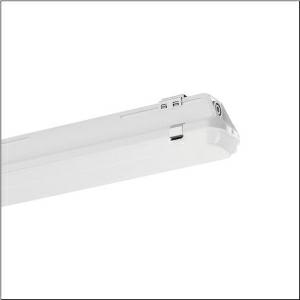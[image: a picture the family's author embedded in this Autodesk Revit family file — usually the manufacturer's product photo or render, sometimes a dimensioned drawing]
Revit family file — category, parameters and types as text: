
# Revit family: monsun_r__11_facade_51ff40mp460h_34d2
name_source: partatom
category: Lighting Fixtures
units: mm (PartAtom-declared; Revit-internal decimal feet)

## family parameters
Cut with Voids When Loaded = No
Host = Face
Light Source = No
Part Type = Normal
Room Calculation Point = No
Round Connector Dimension = Use Diameter
Shared = No

## types (1)
- --- (1 x LED, 6110 lm, 33.5 W, 4000K)
    Apparent Load = 34 VA
    CIE Flux Codes = 47 77 93 95 100
    Color Rendering = 80
    Color Temperature = 4000K
    Default Elevation = 1800 mm
    Description = Monsun® 11 facade, damp-proof luminaire, chain hanger, primary optical cover: enclosure, of PMMA, light emission: direct distribution, primary light characteristic: symmetric, installation type: surface-mounted, horizontal mounting, vertical mounting, LED, rated luminous flux: 6.110lm, luminous efficacy: 182lm/W, light colour: 840, colour temperature: 4000K, control gear: ON/OFF Multilumen, with terminal, 3-pole, max. 2.5mm², mains connection: 220..240V, AC, 50/60Hz, rated input power: 34W, luminaire housing, of glass-fibre reinforced polyester, uncoated, bright grey, incl. chain hanger, for cables, Ø 8.4..12mm, with climate membrane, length: 1.590mm, width: 90mm, height: 88mm, clip for enclosure, of stainless steel (V2A), ceiling mounting element, of stainless steel (V2A), chain hanger, of stainless steel (V2A), protection rating (complete): IP66, insulation class (complete): insulation class I (protective earthing), certification: CE, ENEC, VDE, UKCA, protection symbol: D, impact resistance: IK06, permissible operating ambient temperature: -35..+50°C, standard: EN 50419, EN 60598-2-1, contact your sales advisor before using the luminaires in applications with unclear chemical exposure, large temperature fluctuations or condensation-forming humidity, LABS conformity tested according to VDMA 24364:2018-05, exposed outdoor area, packaging unit: 1 piece
    Height = 89 mm
    Lamp = 1 x LED
    Lamp Light Flux = 6110 lm
    Lamp Power = 33.5 W
    Lamp count = 1
    Length = 1590 mm
    Luminous efficacy = 182 lm/W
    Manufacturer = Siteco
    ModVariant = No
    Model = 51FF40MP460H
    Mounting Place = Ceiling
    Mounting Type = Surface mounted
    Number of Poles = 1
    OnlyDefault = Yes
    Power Factor = 1
    Product Name = Monsun® 11 facade
    Product group = damp-proof luminaire
    ProductGroupID = 300
    Protection Class = Protection class I
    Protection Degree = IP 66
    RLX_Detail_Level = 1
    RLX_Emergency_Light_Flux = 0 lm
    RLX_Emergency_Type = 0
    RLX_Emergency_Type_DB = No
    RlxData = <blob elided: 89549 chars, md5=bd69382b>
    Socket = socket
    Standby Power = 0 W
    System Light Flux = 6110 lm
    System Power = 34 W
    Type Comments = factory setting: luminous flux: 100 % | (A | C | E) | 77 mA
    Type Image = l_1349237.jpg
    URL = http://relux.com
    VarID = @adj_199702
    Voltage = 0 V
    Weight = 0.00 kg
    Width = 90 mm

## geometry (parser evidence)
native form markers: Blend x4, Sweep x12
no freeform markers — native parametric forms only
